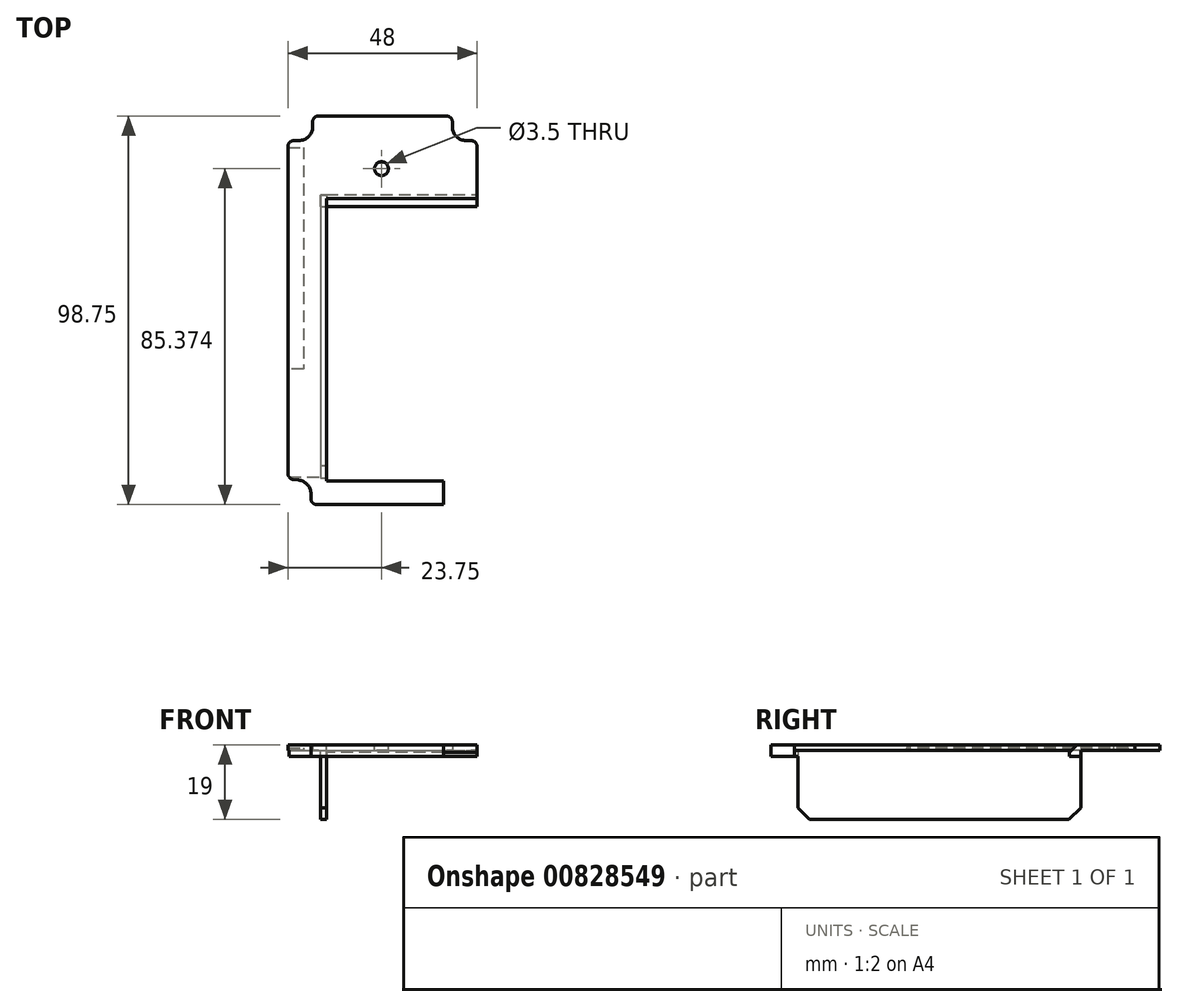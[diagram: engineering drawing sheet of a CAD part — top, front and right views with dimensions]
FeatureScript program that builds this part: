
annotation { "Feature Type Name" : "Feature", "Feature Type Description" : "" }
export const myFeature = defineFeature(function(context is Context, id is Id, definition is map)
    precondition{}
    {
        {
            var Q0;
            Q0=qCreatedBy(makeId("Top.planeOp"),FACE);
            var sketch = newSketch(context, id + "F0", { "sketchPlane" : qUnion([Q0])});
            skPoint(sketch, "E0.middle", {"position": v(0, 0) * mm});
            skLineSegment(sketch, "E1.0", {"start": v(-23.75, 49.2) * mm, "end": v(24.25, 49.2) * mm});
            skLineSegment(sketch, "E1.1", {"start": v(-23.75, 49.2) * mm, "end": v(-23.75, -49.54) * mm});
            skLineSegment(sketch, "E1.2", {"start": v(-23.75, -49.54) * mm, "end": v(24.25, -49.54) * mm});
            skLineSegment(sketch, "E1.3", {"start": v(24.25, 49.2) * mm, "end": v(24.25, 26.2) * mm});
            skLineSegment(sketch, "E2", {"start": v(-23.75, 42.96) * mm, "end": v(-21, 42.96) * mm});
            skLineSegment(sketch, "E3", {"start": v(21.5, -43.3) * mm, "end": v(24.25, -43.3) * mm});
            skLineSegment(sketch, "E4", {"start": v(-17.5, 46.46) * mm, "end": v(-17.5, 49.2) * mm});
            skLineSegment(sketch, "E5", {"start": v(18, -46.8) * mm, "end": v(18, -49.54) * mm});
            skArc(sketch, "E6.filletArc", {"start": v(-21, 42.96) * mm, "mid": v(-18.53, 43.98) * mm, "end": v(-17.5, 46.46) * mm});
            skArc(sketch, "E7.filletArc", {"start": v(21.5, -43.3) * mm, "mid": v(19.03, -44.32) * mm, "end": v(18, -46.8) * mm});
            skLineSegment(sketch, "E8", {"start": v(-23.75, -43) * mm, "end": v(-21.02, -43.31) * mm});
            skLineSegment(sketch, "E9", {"start": v(-17.92, -49.54) * mm, "end": v(-17.92, -46.8) * mm});
            skLineSegment(sketch, "E10", {"start": v(21.5, 42.96) * mm, "end": v(24.25, 42.96) * mm});
            skLineSegment(sketch, "E11", {"start": v(18, 49.2) * mm, "end": v(18, 46.46) * mm});
            skPoint(sketch, "E12.newPointA", {"position": v(18, -49.54) * mm});
            skArc(sketch, "E12.filletArc", {"start": v(18, 46.46) * mm, "mid": v(19.03, 43.98) * mm, "end": v(21.5, 42.96) * mm});
            skPoint(sketch, "E13.newPointA", {"position": v(24.25, -48.54) * mm});
            skArc(sketch, "E13.filletArc", {"start": v(-17.92, -46.8) * mm, "mid": v(-18.8, -44.46) * mm, "end": v(-21.02, -43.31) * mm});
            skPoint(sketch, "E14.orphan", {"position": v(26, 51.5) * mm});
            skPoint(sketch, "E15.orphan", {"position": v(-26, 51.5) * mm});
            skPoint(sketch, "E16.orphan", {"position": v(-26, -51.5) * mm});
            skPoint(sketch, "E0.right.end.orphan", {"position": v(26, -51.5) * mm});
            skLineSegment(sketch, "E17", {"start": v(-14, 26.2) * mm, "end": v(24.25, 26.2) * mm});
            skLineSegment(sketch, "E18", {"start": v(-14, 26.2) * mm, "end": v(-14, -42.54) * mm});
            skLineSegment(sketch, "E19", {"start": v(-23.75, -42.54) * mm, "end": v(24.25, -42.54) * mm});
            skLineSegment(sketch, "E20", {"start": v(15.75, -42.54) * mm, "end": v(15.75, -49.54) * mm});
            skLineSegment(sketch, "E21.trimOffspring", {"start": v(24.25, -43.3) * mm, "end": v(24.25, -49.54) * mm});
            skLineSegment(sketch, "E22", {"start": v(24.25, -42.54) * mm, "end": v(24.25, -43.3) * mm});
            skLineSegment(sketch, "E23", {"start": v(-14, 29.2) * mm, "end": v(24.25, 29.2) * mm});
            skLineSegment(sketch, "E24", {"start": v(-14, 26.2) * mm, "end": v(-14, 29.2) * mm});
            skSolve(sketch);
        }
        {
            var Q0;
            {var subQ3=sQuery(id+"F0.wireOp",EDGE,"E9");Q0=makeQuery(id+"F0.imprint","IMPRINT",FACE,{"disambiguationData":[TD([[makeQuery(id+"F0.imprint","IMPRINT",EDGE,{"derivedFrom":subQ3}),-1.0]])]});}
            var Q1;
            {var subQ8=sQuery(id+"F0.wireOp",EDGE,"E2");Q1=makeQuery(id+"F0.imprint","IMPRINT",FACE,{"disambiguationData":[TD([[makeQuery(id+"F0.imprint","IMPRINT",EDGE,{"derivedFrom":subQ8}),-1.0]])]});}
            var Q2;
            {var subQ0=sQuery(id+"F0.wireOp",EDGE,"E17");Q2=makeQuery(id+"F0.imprint","IMPRINT",FACE,{"disambiguationData":[TD([[makeQuery(id+"F0.imprint","IMPRINT",EDGE,{"derivedFrom":subQ0}),1.0]])]});}
            extrude(context, id + "F1", {"entities" : qUnion([Q0, Q1, Q2]), "depth" : 1.5 * mm, "offsetDistance" : 25 * mm});
        }
        {
            var Q0;
            {var subQ3=sQuery(id+"F0.wireOp",EDGE,"E9");Q0=makeQuery(id+"F0.imprint","IMPRINT",FACE,{"disambiguationData":[TD([[makeQuery(id+"F0.imprint","IMPRINT",EDGE,{"derivedFrom":subQ3}),-1.0]])]});}
            var Q1;
            {var subQ0=sQuery(id+"F0.wireOp",EDGE,"E17");Q1=makeQuery(id+"F0.imprint","IMPRINT",FACE,{"disambiguationData":[TD([[makeQuery(id+"F0.imprint","IMPRINT",EDGE,{"derivedFrom":subQ0}),1.0]])]});}
            extrude(context, id + "F2", {"entities" : qUnion([Q0, Q1]), "oppositeDirection" : true, "depth" : 1.5 * mm, "offsetDistance" : 25 * mm});
        }
        {
            var Q0;
            Q0=makeQuery(id+"F1.opExtrude","SWEPT_BODY",BODY,{"disambiguationData":[OSD([sQuery(id+"F0.wireOp",EDGE,"E1.0"),sQuery(id+"F0.wireOp",EDGE,"E1.1"),sQuery(id+"F0.wireOp",EDGE,"E1.2"),sQuery(id+"F0.wireOp",EDGE,"E1.3"),sQuery(id+"F0.wireOp",EDGE,"E2"),sQuery(id+"F0.wireOp",EDGE,"E4"),sQuery(id+"F0.wireOp",EDGE,"E5"),sQuery(id+"F0.wireOp",EDGE,"E6.filletArc"),sQuery(id+"F0.wireOp",EDGE,"E7.filletArc"),sQuery(id+"F0.wireOp",EDGE,"E8"),sQuery(id+"F0.wireOp",EDGE,"E9"),sQuery(id+"F0.wireOp",EDGE,"E10"),sQuery(id+"F0.wireOp",EDGE,"E11"),sQuery(id+"F0.wireOp",EDGE,"E12.filletArc"),sQuery(id+"F0.wireOp",EDGE,"E13.filletArc"),sQuery(id+"F0.wireOp",EDGE,"E17"),sQuery(id+"F0.wireOp",EDGE,"E18"),sQuery(id+"F0.wireOp",EDGE,"E19")])]});
            var Q1;
            Q1=makeQuery(id+"F2.opExtrude","SWEPT_BODY",BODY,{"disambiguationData":[OSD([sQuery(id+"F0.wireOp",EDGE,"E1.2"),sQuery(id+"F0.wireOp",EDGE,"E9"),sQuery(id+"F0.wireOp",EDGE,"E13.filletArc"),sQuery(id+"F0.wireOp",EDGE,"E19"),sQuery(id+"F0.wireOp",EDGE,"E20")])]});
            var Q2;
            Q2=makeQuery(id+"F2.opExtrude","SWEPT_BODY",BODY,{"disambiguationData":[OSD([sQuery(id+"F0.wireOp",EDGE,"E1.3"),sQuery(id+"F0.wireOp",EDGE,"E17"),sQuery(id+"F0.wireOp",EDGE,"E23"),sQuery(id+"F0.wireOp",EDGE,"E24")])]});
            booleanBodies(context, id + "F3", {"operationType" : BooleanOperationType.UNION, "tools" : qUnion([Q0, Q1, Q2])});
        }
        {
            var Q0;
            {var subQ5=sQuery(id+"F0.wireOp",EDGE,"E2");Q0=makeQuery(id+"F0.imprint","IMPRINT",FACE,{"disambiguationData":[TD([[makeQuery(id+"F0.imprint","IMPRINT",EDGE,{"derivedFrom":subQ5}),-1.0]])]});}
            var sketch = newSketch(context, id + "F4", { "sketchPlane" : qUnion([Q0])});
            skLineSegment(sketch, "E25", {"start": v(-27.8, 41.24) * mm, "end": v(-19.8, 41.24) * mm});
            skLineSegment(sketch, "E26", {"start": v(-19.8, 41.24) * mm, "end": v(-19.8, -15.1) * mm});
            skLineSegment(sketch, "E27", {"start": v(-19.8, -15.1) * mm, "end": v(-27.95, -15.1) * mm});
            skLineSegment(sketch, "E28", {"start": v(-27.95, -15.1) * mm, "end": v(-27.8, 41.24) * mm});
            skSolve(sketch);
        }
        {
            var Q0;
            Q0 = qSketchRegion(id + "F4", true);
            extrude(context, id + "F5", {"entities" : qUnion([Q0]), "operationType" : NewBodyOperationType.REMOVE, "depth" : .75 * mm, "offsetDistance" : 25 * mm});
        }
        {
            var Q0;
            Q0=makeQuery(id+"F1.opExtrude","SWEPT_EDGE",EDGE,{"disambiguationData":[OSD([sQuery(id+"F0.wireOp",EDGE,"E1.0"),sQuery(id+"F0.wireOp",EDGE,"E4")])]});
            var Q1;
            Q1=makeQuery(id+"F1.opExtrude","SWEPT_EDGE",EDGE,{"disambiguationData":[OSD([sQuery(id+"F0.wireOp",EDGE,"E1.1"),sQuery(id+"F0.wireOp",EDGE,"E2")])]});
            var Q2;
            Q2=makeQuery(id+"F1.opExtrude","SWEPT_EDGE",EDGE,{"disambiguationData":[OSD([sQuery(id+"F0.wireOp",EDGE,"E1.0"),sQuery(id+"F0.wireOp",EDGE,"E11")])]});
            var Q3;
            Q3=makeQuery(id+"F1.opExtrude","SWEPT_EDGE",EDGE,{"disambiguationData":[OSD([sQuery(id+"F0.wireOp",EDGE,"E1.3"),sQuery(id+"F0.wireOp",EDGE,"E10")])]});
            var Q4;
            {var subQ0=sQuery(id+"F0.wireOp",EDGE,"E8");var subQ1=sQuery(id+"F0.wireOp",EDGE,"E1.1");Q4=makeQuery(id+"F3.opBoolean","MERGE",EDGE,{"derivedFrom":[makeQuery(id+"F1.opExtrude","SWEPT_EDGE",EDGE,{"disambiguationData":[OSD([subQ1,subQ0])]}),makeQuery(id+"F2.opExtrude","SWEPT_EDGE",EDGE,{"disambiguationData":[OSD([subQ1,subQ0])]})]});}
            var Q5;
            {var subQ0=sQuery(id+"F0.wireOp",EDGE,"E9");var subQ1=sQuery(id+"F0.wireOp",EDGE,"E1.2");Q5=makeQuery(id+"F3.opBoolean","MERGE",EDGE,{"derivedFrom":[makeQuery(id+"F1.opExtrude","SWEPT_EDGE",EDGE,{"disambiguationData":[OSD([subQ1,subQ0])]}),makeQuery(id+"F2.opExtrude","SWEPT_EDGE",EDGE,{"disambiguationData":[OSD([subQ1,subQ0])]})]});}
            fillet(context, id + "F6", {"entities" : qUnion([Q0, Q1, Q2, Q3, Q4, Q5]), "radius" : 1.5 * mm, "tangentPropagation" : true, "allowEdgeOverflow" : false});
        }
        {
            var Q0;
            Q0=qCreatedBy(makeId("Top.planeOp"),FACE);
            var sketch = newSketch(context, id + "F7", { "sketchPlane" : qUnion([Q0])});
            skLineSegment(sketch, "E29.bottom", {"start": v(-15.48, 29.17) * mm, "end": v(-13.98, 29.17) * mm});
            skLineSegment(sketch, "E29.top", {"start": v(-15.48, -42.76) * mm, "end": v(-13.98, -42.76) * mm});
            skLineSegment(sketch, "E29.left", {"start": v(-15.48, 29.17) * mm, "end": v(-15.48, -42.76) * mm});
            skLineSegment(sketch, "E29.right", {"start": v(-13.98, 29.17) * mm, "end": v(-13.98, -42.76) * mm});
            skSolve(sketch);
        }
        {
            var Q0;
            Q0 = qSketchRegion(id + "F7", true);
            extrude(context, id + "F8", {"entities" : qUnion([Q0]), "oppositeDirection" : true, "depth" : 17.5 * mm, "offsetDistance" : 25 * mm});
        }
        {
            var Q0;
            Q0=makeQuery(id+"F1.opExtrude","SWEPT_BODY",BODY,{"disambiguationData":[OSD([sQuery(id+"F0.wireOp",EDGE,"E1.0"),sQuery(id+"F0.wireOp",EDGE,"E1.1"),sQuery(id+"F0.wireOp",EDGE,"E1.2"),sQuery(id+"F0.wireOp",EDGE,"E1.3"),sQuery(id+"F0.wireOp",EDGE,"E2"),sQuery(id+"F0.wireOp",EDGE,"E4"),sQuery(id+"F0.wireOp",EDGE,"E6.filletArc"),sQuery(id+"F0.wireOp",EDGE,"E8"),sQuery(id+"F0.wireOp",EDGE,"E9"),sQuery(id+"F0.wireOp",EDGE,"E10"),sQuery(id+"F0.wireOp",EDGE,"E11"),sQuery(id+"F0.wireOp",EDGE,"E12.filletArc"),sQuery(id+"F0.wireOp",EDGE,"E13.filletArc"),sQuery(id+"F0.wireOp",EDGE,"E17"),sQuery(id+"F0.wireOp",EDGE,"E18"),sQuery(id+"F0.wireOp",EDGE,"E19"),sQuery(id+"F0.wireOp",EDGE,"E20")])]});
            var Q1;
            Q1=makeQuery(id+"F8.opExtrude","SWEPT_BODY",BODY,{"disambiguationData":[OSD([sQuery(id+"F7.wireOp",EDGE,"E29.bottom"),sQuery(id+"F7.wireOp",EDGE,"E29.top"),sQuery(id+"F7.wireOp",EDGE,"E29.left"),sQuery(id+"F7.wireOp",EDGE,"E29.right")])]});
            booleanBodies(context, id + "F9", {"operationType" : BooleanOperationType.UNION, "tools" : qUnion([Q0, Q1])});
        }
        {
            var Q0;
            Q0=makeQuery(id+"F8.opExtrude","CAP_EDGE",EDGE,{"disambiguationData":[OSD([sQuery(id+"F7.wireOp",EDGE,"E29.top")])],"isStart":false});
            var Q1;
            Q1=makeQuery(id+"F8.opExtrude","CAP_EDGE",EDGE,{"disambiguationData":[OSD([sQuery(id+"F7.wireOp",EDGE,"E29.bottom")])],"isStart":false});
            chamfer(context, id + "F10", {"entities" : qUnion([Q0, Q1]), "width" : 3 * mm, "tangentPropagation" : true});
        }
        {
            var Q0;
            Q0=makeQuery(id+"F1.opExtrude","SWEPT_BODY",BODY,{"disambiguationData":[OSD([sQuery(id+"F0.wireOp",EDGE,"E1.0"),sQuery(id+"F0.wireOp",EDGE,"E1.1"),sQuery(id+"F0.wireOp",EDGE,"E1.2"),sQuery(id+"F0.wireOp",EDGE,"E1.3"),sQuery(id+"F0.wireOp",EDGE,"E2"),sQuery(id+"F0.wireOp",EDGE,"E4"),sQuery(id+"F0.wireOp",EDGE,"E6.filletArc"),sQuery(id+"F0.wireOp",EDGE,"E8"),sQuery(id+"F0.wireOp",EDGE,"E9"),sQuery(id+"F0.wireOp",EDGE,"E10"),sQuery(id+"F0.wireOp",EDGE,"E11"),sQuery(id+"F0.wireOp",EDGE,"E12.filletArc"),sQuery(id+"F0.wireOp",EDGE,"E13.filletArc"),sQuery(id+"F0.wireOp",EDGE,"E17"),sQuery(id+"F0.wireOp",EDGE,"E18"),sQuery(id+"F0.wireOp",EDGE,"E19"),sQuery(id+"F0.wireOp",EDGE,"E20")])]});
            transform(context, id + "F11", {"entities" : qUnion([Q0]), "transformType" : TransformType.TRANSLATION_3D, "dx" : 0 * mm, "dy" : 0 * mm, "dz" : 0 * mm, "makeCopy" : true});
        }
        {
            var Q0;
            Q0=makeQuery(id+"F11.opPattern","COPY",BODY,{"derivedFrom":makeQuery(id+"F1.opExtrude","SWEPT_BODY",BODY,{"disambiguationData":[OSD([sQuery(id+"F0.wireOp",EDGE,"E1.0"),sQuery(id+"F0.wireOp",EDGE,"E1.1"),sQuery(id+"F0.wireOp",EDGE,"E1.2"),sQuery(id+"F0.wireOp",EDGE,"E1.3"),sQuery(id+"F0.wireOp",EDGE,"E2"),sQuery(id+"F0.wireOp",EDGE,"E4"),sQuery(id+"F0.wireOp",EDGE,"E6.filletArc"),sQuery(id+"F0.wireOp",EDGE,"E8"),sQuery(id+"F0.wireOp",EDGE,"E9"),sQuery(id+"F0.wireOp",EDGE,"E10"),sQuery(id+"F0.wireOp",EDGE,"E11"),sQuery(id+"F0.wireOp",EDGE,"E12.filletArc"),sQuery(id+"F0.wireOp",EDGE,"E13.filletArc"),sQuery(id+"F0.wireOp",EDGE,"E17"),sQuery(id+"F0.wireOp",EDGE,"E18"),sQuery(id+"F0.wireOp",EDGE,"E19"),sQuery(id+"F0.wireOp",EDGE,"E20")])]}),"instanceName":"1"});
            deleteBodies(context, id + "F12", {"entities" : qUnion([Q0])});
        }
        {
            var Q0;
            Q0=makeQuery(id+"F1.opExtrude","CAP_FACE",FACE,{"disambiguationData":[OSD([sQuery(id+"F0.wireOp",EDGE,"E1.0"),sQuery(id+"F0.wireOp",EDGE,"E1.1"),sQuery(id+"F0.wireOp",EDGE,"E1.2"),sQuery(id+"F0.wireOp",EDGE,"E1.3"),sQuery(id+"F0.wireOp",EDGE,"E2"),sQuery(id+"F0.wireOp",EDGE,"E4"),sQuery(id+"F0.wireOp",EDGE,"E6.filletArc"),sQuery(id+"F0.wireOp",EDGE,"E8"),sQuery(id+"F0.wireOp",EDGE,"E9"),sQuery(id+"F0.wireOp",EDGE,"E10"),sQuery(id+"F0.wireOp",EDGE,"E11"),sQuery(id+"F0.wireOp",EDGE,"E12.filletArc"),sQuery(id+"F0.wireOp",EDGE,"E13.filletArc"),sQuery(id+"F0.wireOp",EDGE,"E17"),sQuery(id+"F0.wireOp",EDGE,"E18"),sQuery(id+"F0.wireOp",EDGE,"E19"),sQuery(id+"F0.wireOp",EDGE,"E20")])],"isStart":false});
            var sketch = newSketch(context, id + "F13", { "sketchPlane" : qUnion([Q0])});
            skCircle(sketch, "E30", {"center": v(0, 35.83) * mm, "radius": 1.75 * mm});
            skSolve(sketch);
        }
        {
            var Q0;
            Q0 = qSketchRegion(id + "F13", true);
            extrude(context, id + "F14", {"entities" : qUnion([Q0]), "operationType" : NewBodyOperationType.REMOVE, "oppositeDirection" : true, "depth" : 25 * mm, "offsetDistance" : 25 * mm});
        }
        {
            var Q0;
            {var subQ1=sQuery(id+"F0.wireOp",EDGE,"E19");var subQ7=sQuery(id+"F0.wireOp",EDGE,"E18");Q0=makeQuery(id+"F9.opBoolean","SPLIT",FACE,{"disambiguationData":[TD([makeQuery(id+"F1.opExtrude","SWEPT_FACE",FACE,{"disambiguationData":[OSD([subQ7])]})])],"derivedFrom":makeQuery(id+"F3.opBoolean","MERGE",FACE,{"derivedFrom":[makeQuery(id+"F1.opExtrude","SWEPT_FACE",FACE,{"disambiguationData":[OSD([subQ1])]}),makeQuery(id+"F2.opExtrude","SWEPT_FACE",FACE,{"disambiguationData":[OSD([subQ1])]})]})});}
            extrude(context, id + "F15", {"entities" : qUnion([Q0]), "operationType" : NewBodyOperationType.REMOVE, "oppositeDirection" : true, "depth" : 1 * mm, "offsetDistance" : 25 * mm});
        }
        {
            var Q0;
            Q0=makeQuery(id+"F1.opExtrude","CAP_EDGE",EDGE,{"disambiguationData":[OSD([sQuery(id+"F0.wireOp",EDGE,"E17")])],"isStart":false});
            var Q1;
            {var subQ0=sQuery(id+"F0.wireOp",EDGE,"E19");var subQ1=sQuery(id+"F0.wireOp",EDGE,"E18");Q1=makeQuery(id+"F15.boolean.opBoolean","MERGE",EDGE,{"derivedFrom":[makeQuery(id+"F1.opExtrude","CAP_EDGE",EDGE,{"disambiguationData":[OSD([subQ1])],"isStart":false})],"fromTools":[makeQuery(id+"F15.opExtrude","SWEPT_EDGE",EDGE,{"disambiguationData":[OSD([subQ1,subQ0]),TDD([makeQuery(id+"F1.opExtrude","CAP_VERTEX",VERTEX,{"disambiguationData":[OSD([subQ1,subQ0])],"isStart":false})])]})]});}
            var Q2;
            {var subQ0=sQuery(id+"F0.wireOp",EDGE,"E19");Q2=makeQuery(id+"F15.boolean.opBoolean","COPY",EDGE,{"derivedFrom":makeQuery(id+"F15.opExtrude","CAP_EDGE",EDGE,{"disambiguationData":[OSD([subQ0]),TDD([makeQuery(id+"F1.opExtrude","CAP_EDGE",EDGE,{"disambiguationData":[OSD([subQ0])],"isStart":false})])],"isStart":false})});}
            chamfer(context, id + "F16", {"entities" : qUnion([Q0, Q1, Q2]), "width" : 2 * mm, "tangentPropagation" : true});
        }
    });
